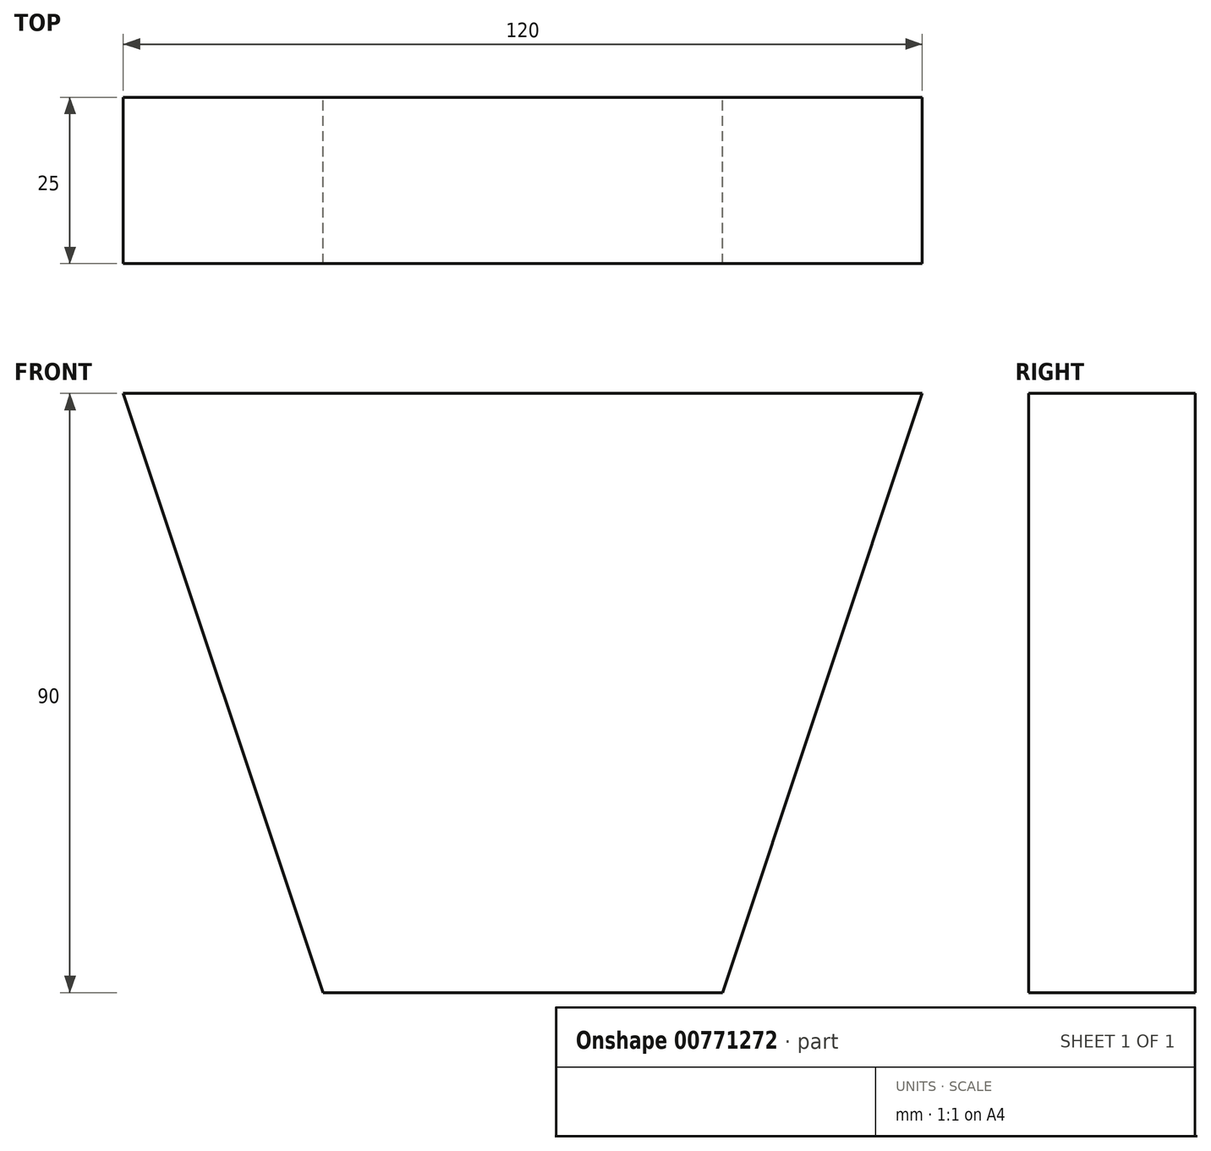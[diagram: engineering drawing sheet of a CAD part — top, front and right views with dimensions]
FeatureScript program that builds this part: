
annotation { "Feature Type Name" : "Feature", "Feature Type Description" : "" }
export const myFeature = defineFeature(function(context is Context, id is Id, definition is map)
    precondition{}
    {
        {
            var Q0;
            Q0=qCreatedBy(makeId("Front.planeOp"),FACE);
            var sketch = newSketch(context, id + "F0", { "sketchPlane" : qUnion([Q0])});
            skLineSegment(sketch, "E0", {"start": v(0, 0) * mm, "end": v(60, 0) * mm});
            skLineSegment(sketch, "E1", {"start": v(0, 0) * mm, "end": v(0, -90) * mm});
            skLineSegment(sketch, "E2", {"start": v(0, -90) * mm, "end": v(30, -90) * mm});
            skLineSegment(sketch, "E3", {"start": v(30, -90) * mm, "end": v(60, 0) * mm});
            skLineSegment(sketch, "E4", {"start": v(0, 0) * mm, "end": v(-60, 0) * mm});
            skLineSegment(sketch, "E5", {"start": v(0, -90) * mm, "end": v(-30, -90) * mm});
            skLineSegment(sketch, "E6", {"start": v(-30, -90) * mm, "end": v(-60, 0) * mm});
            skSolve(sketch);
        }
        {
            var Q0;
            Q0=makeQuery(id+"F0.imprint","IMPRINT",FACE,{"disambiguationData":[TD([[makeQuery(id+"F0.imprint","IMPRINT",EDGE,{"derivedFrom":sQuery(id+"F0.wireOp",EDGE,"E1")}),-1.0]])]});
            var Q1;
            Q1=makeQuery(id+"F0.imprint","IMPRINT",FACE,{"disambiguationData":[TD([[makeQuery(id+"F0.imprint","IMPRINT",EDGE,{"derivedFrom":sQuery(id+"F0.wireOp",EDGE,"E1")}),1.0]])]});
            extrude(context, id + "F1", {"entities" : qUnion([Q0, Q1]), "depth" : 25 * mm, "offsetDistance" : 25 * mm});
        }
    });
